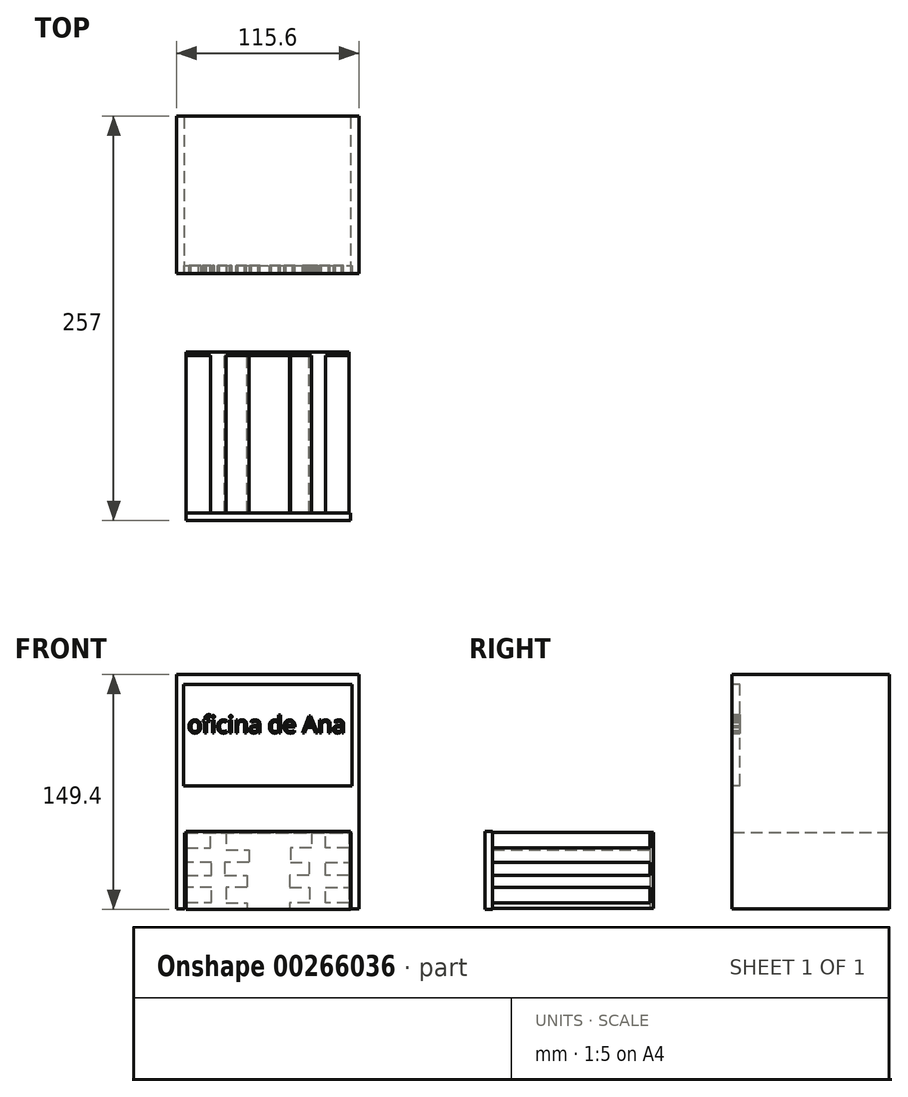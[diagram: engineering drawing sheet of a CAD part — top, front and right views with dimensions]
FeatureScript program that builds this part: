
annotation { "Feature Type Name" : "Feature", "Feature Type Description" : "" }
export const myFeature = defineFeature(function(context is Context, id is Id, definition is map)
    precondition{}
    {
        {
            var Q0;
            Q0=qCreatedBy(makeId("Front.planeOp"),FACE);
            var sketch = newSketch(context, id + "F0", { "sketchPlane" : qUnion([Q0])});
            skLineSegment(sketch, "E0.bottom", {"start": v(-57.8, -74.47) * mm, "end": v(57.8, -74.47) * mm});
            skLineSegment(sketch, "E0.top", {"start": v(-57.8, 74.47) * mm, "end": v(57.8, 74.47) * mm});
            skLineSegment(sketch, "E0.left", {"start": v(-57.8, -74.47) * mm, "end": v(-57.8, 74.47) * mm});
            skLineSegment(sketch, "E0.right", {"start": v(57.8, -74.47) * mm, "end": v(57.8, 74.47) * mm});
            skPoint(sketch, "E0.middle", {"position": v(0, 0) * mm});
            skSolve(sketch);
        }
        {
            var Q0;
            Q0 = qSketchRegion(id + "F0", true);
            extrude(context, id + "F1", {"entities" : qUnion([Q0]), "endBound" : BoundingType.SYMMETRIC, "depth" : 100 * mm});
        }
        {
            var Q0;
            Q0=makeQuery(id+"F1.opExtrude","CAP_FACE",FACE,{"disambiguationData":[OSD([sQuery(id+"F0.wireOp",EDGE,"E0.bottom"),sQuery(id+"F0.wireOp",EDGE,"E0.top"),sQuery(id+"F0.wireOp",EDGE,"E0.left"),sQuery(id+"F0.wireOp",EDGE,"E0.right")])],"isStart":false});
            var sketch = newSketch(context, id + "F2", { "sketchPlane" : qUnion([Q0])});
            skLineSegment(sketch, "E1.bottom", {"start": v(-53.37, 3.6) * mm, "end": v(53.37, 3.6) * mm});
            skLineSegment(sketch, "E1.top", {"start": v(-53.37, 68.07) * mm, "end": v(53.37, 68.07) * mm});
            skLineSegment(sketch, "E1.left", {"start": v(-53.37, 3.6) * mm, "end": v(-53.37, 68.07) * mm});
            skLineSegment(sketch, "E1.right", {"start": v(53.37, 3.6) * mm, "end": v(53.37, 68.07) * mm});
            skPoint(sketch, "E1.middle", {"position": v(0, 35.84) * mm});
            skSolve(sketch);
        }
        {
            var Q0;
            Q0 = qSketchRegion(id + "F2", true);
            extrude(context, id + "F3", {"entities" : qUnion([Q0]), "operationType" : NewBodyOperationType.REMOVE, "oppositeDirection" : true, "depth" : 5 * mm});
        }
        {
            var Q0;
            Q0=makeQuery(id+"F3.boolean.opBoolean","COPY",FACE,{"derivedFrom":makeQuery(id+"F3.opExtrude","CAP_FACE",FACE,{"disambiguationData":[OSD([sQuery(id+"F2.wireOp",EDGE,"E1.bottom"),sQuery(id+"F2.wireOp",EDGE,"E1.top"),sQuery(id+"F2.wireOp",EDGE,"E1.left"),sQuery(id+"F2.wireOp",EDGE,"E1.right")])],"isStart":false})});
            var sketch = newSketch(context, id + "F4", { "sketchPlane" : qUnion([Q0])});
            skText(sketch, "E2", { "text": "oficina de Ana", "fontName": "OpenSans-Regular.ttf"});
            const initialGuessF4  = {"E2": [-0.05089, 0.03716, 1, 0, 0.01095]};
            skSetInitialGuess(sketch, initialGuessF4);
            skSolve(sketch);
        }
        {
            var Q0;
            Q0 = qSketchRegion(id + "F4", true);
            extrude(context, id + "F5", {"entities" : qUnion([Q0]), "operationType" : NewBodyOperationType.ADD, "depth" : 5 * mm});
        }
        {
            var Q0;
            Q0=makeQuery(id+"F1.opExtrude","CAP_FACE",FACE,{"disambiguationData":[OSD([sQuery(id+"F0.wireOp",EDGE,"E0.bottom"),sQuery(id+"F0.wireOp",EDGE,"E0.top"),sQuery(id+"F0.wireOp",EDGE,"E0.left"),sQuery(id+"F0.wireOp",EDGE,"E0.right")])],"isStart":false});
            var sketch = newSketch(context, id + "F6", { "sketchPlane" : qUnion([Q0])});
            skLineSegment(sketch, "E3.bottom", {"start": v(-52.71, -83.74) * mm, "end": v(52.71, -83.74) * mm});
            skLineSegment(sketch, "E3.top", {"start": v(-52.71, -26.2) * mm, "end": v(52.71, -26.2) * mm});
            skLineSegment(sketch, "E3.left", {"start": v(-52.71, -83.74) * mm, "end": v(-52.71, -26.2) * mm});
            skLineSegment(sketch, "E3.right", {"start": v(52.71, -83.74) * mm, "end": v(52.71, -26.2) * mm});
            skPoint(sketch, "E3.middle", {"position": v(0, -54.97) * mm});
            skSolve(sketch);
        }
        {
            var Q0;
            Q0 = qSketchRegion(id + "F6", true);
            extrude(context, id + "F7", {"entities" : qUnion([Q0]), "operationType" : NewBodyOperationType.REMOVE, "endBound" : BoundingType.THROUGH_ALL, "oppositeDirection" : true, "depth" : 25 * mm});
        }
        {
            var Q0;
            Q0=makeQuery(id+"F1.opExtrude","CAP_FACE",FACE,{"disambiguationData":[OSD([sQuery(id+"F0.wireOp",EDGE,"E0.bottom"),sQuery(id+"F0.wireOp",EDGE,"E0.top"),sQuery(id+"F0.wireOp",EDGE,"E0.left"),sQuery(id+"F0.wireOp",EDGE,"E0.right")])],"isStart":false});
            cPlane(context, id + "F8", {"entities" : qUnion([Q0]), "cplaneType" : CPlaneType.OFFSET, "offset" : 50 * mm, "width" : 150 * mm, "height" : 150 * mm});
        }
        {
            var Q0;
            Q0=qCreatedBy(id+"F8.planeOp",FACE);
            var sketch = newSketch(context, id + "F9", { "sketchPlane" : qUnion([Q0])});
            skLineSegment(sketch, "E4.bottom", {"start": v(-51.87, -25.94) * mm, "end": v(51.45, -25.94) * mm});
            skLineSegment(sketch, "E4.top", {"start": v(-51.87, -74.41) * mm, "end": v(51.45, -74.41) * mm});
            skLineSegment(sketch, "E4.left", {"start": v(-51.87, -25.94) * mm, "end": v(-51.87, -74.41) * mm});
            skLineSegment(sketch, "E4.right", {"start": v(51.45, -25.94) * mm, "end": v(51.45, -74.41) * mm});
            skSolve(sketch);
        }
        {
            var Q0;
            Q0 = qSketchRegion(id + "F9", true);
            extrude(context, id + "F10", {"entities" : qUnion([Q0]), "depth" : 2 * mm});
        }
        {
            var Q0;
            Q0=makeQuery(id+"F10.opExtrude","CAP_FACE",FACE,{"disambiguationData":[OSD([sQuery(id+"F9.wireOp",EDGE,"E4.bottom"),sQuery(id+"F9.wireOp",EDGE,"E4.top"),sQuery(id+"F9.wireOp",EDGE,"E4.left"),sQuery(id+"F9.wireOp",EDGE,"E4.right")])],"isStart":false});
            var sketch = newSketch(context, id + "F11", { "sketchPlane" : qUnion([Q0])});
            skLineSegment(sketch, "E5", {"start": v(-51.87, -35.92) * mm, "end": v(-36.37, -35.92) * mm});
            skLineSegment(sketch, "E6", {"start": v(-36.37, -35.92) * mm, "end": v(-36.37, -25.94) * mm});
            skLineSegment(sketch, "E7", {"start": v(-36.37, -25.94) * mm, "end": v(-26.55, -25.94) * mm});
            skLineSegment(sketch, "E8", {"start": v(-26.55, -25.94) * mm, "end": v(-26.55, -37.1) * mm});
            skLineSegment(sketch, "E9", {"start": v(-26.55, -37.1) * mm, "end": v(-12.03, -37.1) * mm});
            skLineSegment(sketch, "E10", {"start": v(-12.03, -37.1) * mm, "end": v(-12.03, -44.95) * mm});
            skLineSegment(sketch, "E11", {"start": v(-12.03, -44.95) * mm, "end": v(-27.34, -44.95) * mm});
            skLineSegment(sketch, "E12", {"start": v(-27.34, -44.95) * mm, "end": v(-27.34, -53.2) * mm});
            skLineSegment(sketch, "E13", {"start": v(-27.34, -53.2) * mm, "end": v(-13.2, -53.2) * mm});
            skLineSegment(sketch, "E14", {"start": v(-13.2, -53.2) * mm, "end": v(-13.2, -61.05) * mm});
            skLineSegment(sketch, "E15", {"start": v(-13.2, -61.05) * mm, "end": v(-26.55, -61.05) * mm});
            skLineSegment(sketch, "E16", {"start": v(-26.55, -61.05) * mm, "end": v(-26.55, -70.87) * mm});
            skLineSegment(sketch, "E17", {"start": v(-26.55, -70.87) * mm, "end": v(-13.2, -70.87) * mm});
            skLineSegment(sketch, "E18", {"start": v(-13.2, -70.87) * mm, "end": v(-13.2, -74.41) * mm});
            skLineSegment(sketch, "E19", {"start": v(-13.2, -74.41) * mm, "end": v(-51.87, -74.41) * mm});
            skLineSegment(sketch, "E20", {"start": v(-51.87, -74.41) * mm, "end": v(-51.87, -70.47) * mm});
            skLineSegment(sketch, "E21", {"start": v(-51.87, -70.47) * mm, "end": v(-35.59, -70.47) * mm});
            skLineSegment(sketch, "E22", {"start": v(-35.59, -70.47) * mm, "end": v(-35.59, -61.05) * mm});
            skLineSegment(sketch, "E23", {"start": v(-35.59, -61.05) * mm, "end": v(-51.87, -61.05) * mm});
            skLineSegment(sketch, "E24", {"start": v(-51.87, -61.05) * mm, "end": v(-51.87, -53.2) * mm});
            skLineSegment(sketch, "E25", {"start": v(-51.87, -53.2) * mm, "end": v(-35.59, -53.2) * mm});
            skLineSegment(sketch, "E26", {"start": v(-35.59, -53.2) * mm, "end": v(-35.59, -44.95) * mm});
            skLineSegment(sketch, "E27", {"start": v(-35.59, -44.95) * mm, "end": v(-51.87, -44.95) * mm});
            skLineSegment(sketch, "E28", {"start": v(-51.87, -44.95) * mm, "end": v(-51.87, -35.92) * mm});
            skLineSegment(sketch, "E29", {"start": v(51.45, -35.92) * mm, "end": v(36.67, -35.92) * mm});
            skLineSegment(sketch, "E30", {"start": v(36.67, -35.92) * mm, "end": v(36.67, -25.94) * mm});
            skLineSegment(sketch, "E31", {"start": v(36.67, -25.94) * mm, "end": v(27.64, -25.94) * mm});
            skLineSegment(sketch, "E32", {"start": v(27.64, -25.94) * mm, "end": v(27.64, -35.92) * mm});
            skLineSegment(sketch, "E33", {"start": v(27.64, -35.92) * mm, "end": v(14.29, -35.92) * mm});
            skLineSegment(sketch, "E34", {"start": v(14.29, -35.92) * mm, "end": v(14.29, -44.95) * mm});
            skLineSegment(sketch, "E35", {"start": v(14.29, -44.95) * mm, "end": v(26.07, -44.95) * mm});
            skLineSegment(sketch, "E36", {"start": v(26.07, -44.95) * mm, "end": v(26.07, -53.2) * mm});
            skLineSegment(sketch, "E37", {"start": v(26.07, -53.2) * mm, "end": v(13.9, -53.2) * mm});
            skLineSegment(sketch, "E38", {"start": v(13.9, -53.2) * mm, "end": v(13.9, -61.05) * mm});
            skLineSegment(sketch, "E39", {"start": v(13.9, -61.05) * mm, "end": v(26.46, -61.05) * mm});
            skLineSegment(sketch, "E40", {"start": v(26.46, -61.05) * mm, "end": v(26.46, -70.87) * mm});
            skLineSegment(sketch, "E41", {"start": v(26.46, -70.87) * mm, "end": v(13.9, -70.87) * mm});
            skLineSegment(sketch, "E42", {"start": v(13.9, -70.87) * mm, "end": v(13.9, -74.41) * mm});
            skLineSegment(sketch, "E43", {"start": v(13.9, -74.41) * mm, "end": v(51.45, -74.41) * mm});
            skLineSegment(sketch, "E44", {"start": v(51.45, -74.41) * mm, "end": v(51.45, -70.87) * mm});
            skLineSegment(sketch, "E45", {"start": v(51.45, -70.87) * mm, "end": v(36.67, -70.87) * mm});
            skLineSegment(sketch, "E46", {"start": v(36.67, -70.87) * mm, "end": v(36.67, -61.05) * mm});
            skLineSegment(sketch, "E47", {"start": v(36.67, -61.05) * mm, "end": v(51.45, -61.05) * mm});
            skLineSegment(sketch, "E48", {"start": v(51.45, -61.05) * mm, "end": v(51.45, -53.2) * mm});
            skLineSegment(sketch, "E49", {"start": v(51.45, -53.2) * mm, "end": v(36.67, -53.2) * mm});
            skLineSegment(sketch, "E50", {"start": v(36.67, -53.2) * mm, "end": v(36.67, -44.95) * mm});
            skLineSegment(sketch, "E51", {"start": v(36.67, -44.95) * mm, "end": v(51.45, -44.95) * mm});
            skLineSegment(sketch, "E52", {"start": v(51.45, -44.95) * mm, "end": v(51.45, -35.92) * mm});
            skLineSegment(sketch, "E53", {"start": v(-51.87, -74.41) * mm, "end": v(-13.2, -74.41) * mm});
            skSolve(sketch);
        }
        {
            var Q0;
            Q0 = qSketchRegion(id + "F11", true);
            extrude(context, id + "F12", {"entities" : qUnion([Q0]), "operationType" : NewBodyOperationType.ADD, "depth" : 100 * mm});
        }
        {
            var Q0;
            Q0=makeQuery(id+"F12.opExtrude","CAP_FACE",FACE,{"disambiguationData":[OSD([sQuery(id+"F11.wireOp",EDGE,"E5"),sQuery(id+"F11.wireOp",EDGE,"E6"),sQuery(id+"F11.wireOp",EDGE,"E7"),sQuery(id+"F11.wireOp",EDGE,"E8"),sQuery(id+"F11.wireOp",EDGE,"E9"),sQuery(id+"F11.wireOp",EDGE,"E10"),sQuery(id+"F11.wireOp",EDGE,"E11"),sQuery(id+"F11.wireOp",EDGE,"E12"),sQuery(id+"F11.wireOp",EDGE,"E13"),sQuery(id+"F11.wireOp",EDGE,"E14"),sQuery(id+"F11.wireOp",EDGE,"E15"),sQuery(id+"F11.wireOp",EDGE,"E16"),sQuery(id+"F11.wireOp",EDGE,"E17"),sQuery(id+"F11.wireOp",EDGE,"E18"),sQuery(id+"F11.wireOp",EDGE,"E20"),sQuery(id+"F11.wireOp",EDGE,"E21"),sQuery(id+"F11.wireOp",EDGE,"E22"),sQuery(id+"F11.wireOp",EDGE,"E23"),sQuery(id+"F11.wireOp",EDGE,"E24"),sQuery(id+"F11.wireOp",EDGE,"E25"),sQuery(id+"F11.wireOp",EDGE,"E26"),sQuery(id+"F11.wireOp",EDGE,"E27"),sQuery(id+"F11.wireOp",EDGE,"E28"),sQuery(id+"F11.wireOp",EDGE,"E53")])],"isStart":false});
            var sketch = newSketch(context, id + "F13", { "sketchPlane" : qUnion([Q0])});
            skLineSegment(sketch, "E54.bottom", {"start": v(-51.84, -25.42) * mm, "end": v(52.48, -25.42) * mm});
            skLineSegment(sketch, "E54.top", {"start": v(-51.84, -74.93) * mm, "end": v(52.48, -74.93) * mm});
            skLineSegment(sketch, "E54.left", {"start": v(-51.84, -25.42) * mm, "end": v(-51.84, -74.93) * mm});
            skLineSegment(sketch, "E54.right", {"start": v(52.48, -25.42) * mm, "end": v(52.48, -74.93) * mm});
            skSolve(sketch);
        }
        {
            var Q0;
            Q0 = qSketchRegion(id + "F13", true);
            extrude(context, id + "F14", {"entities" : qUnion([Q0]), "operationType" : NewBodyOperationType.ADD, "depth" : 5 * mm});
        }
    });
